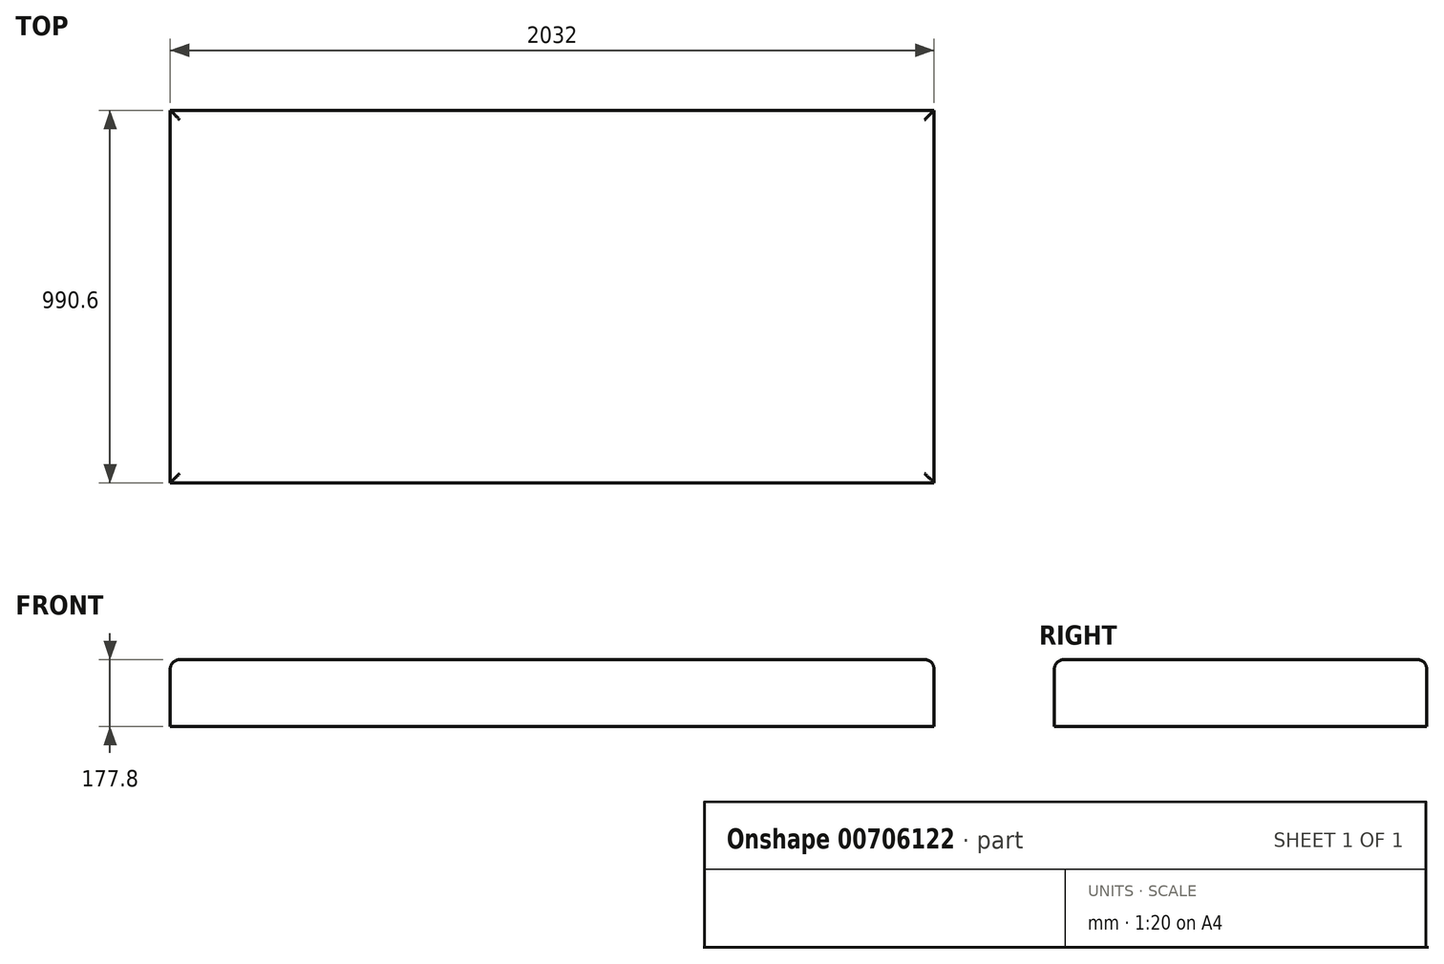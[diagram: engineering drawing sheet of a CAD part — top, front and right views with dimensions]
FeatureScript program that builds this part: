
annotation { "Feature Type Name" : "Feature", "Feature Type Description" : "" }
export const myFeature = defineFeature(function(context is Context, id is Id, definition is map)
    precondition{}
    {
        {
            var Q0;
            Q0=qCreatedBy(makeId("Top.planeOp"),FACE);
            var sketch = newSketch(context, id + "F0", { "sketchPlane" : qUnion([Q0])});
            skLineSegment(sketch, "E0.bottom", {"start": v(0, 0) * mm, "end": v(2032, 0) * mm});
            skLineSegment(sketch, "E0.top", {"start": v(0, 990.6) * mm, "end": v(2032, 990.6) * mm});
            skLineSegment(sketch, "E0.left", {"start": v(0, 0) * mm, "end": v(0, 990.6) * mm});
            skLineSegment(sketch, "E0.right", {"start": v(2032, 0) * mm, "end": v(2032, 990.6) * mm});
            skSolve(sketch);
        }
        {
            var Q0;
            Q0=makeQuery(id+"F0.imprint","IMPRINT",FACE,{"disambiguationData":[TD([[makeQuery(id+"F0.imprint","IMPRINT",EDGE,{"derivedFrom":sQuery(id+"F0.wireOp",EDGE,"E0.bottom")}),1.0]])]});
            extrude(context, id + "F1", {"entities" : qUnion([Q0]), "depth" : 177.8 * mm, "offsetDistance" : 25.4 * mm});
        }
        {
            var Q0;
            Q0=makeQuery(id+"F1.opExtrude","CAP_EDGE",EDGE,{"disambiguationData":[OSD([sQuery(id+"F0.wireOp",EDGE,"E0.left")])],"isStart":false});
            var Q1;
            Q1=makeQuery(id+"F1.opExtrude","CAP_EDGE",EDGE,{"disambiguationData":[OSD([sQuery(id+"F0.wireOp",EDGE,"E0.bottom")])],"isStart":false});
            var Q2;
            Q2=makeQuery(id+"F1.opExtrude","CAP_EDGE",EDGE,{"disambiguationData":[OSD([sQuery(id+"F0.wireOp",EDGE,"E0.top")])],"isStart":false});
            var Q3;
            Q3=makeQuery(id+"F1.opExtrude","CAP_EDGE",EDGE,{"disambiguationData":[OSD([sQuery(id+"F0.wireOp",EDGE,"E0.right")])],"isStart":false});
            fillet(context, id + "F2", {"entities" : qUnion([Q0, Q1, Q2, Q3]), "radius" : 25.4 * mm, "tangentPropagation" : true, "allowEdgeOverflow" : false});
        }
    });
